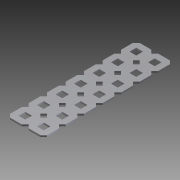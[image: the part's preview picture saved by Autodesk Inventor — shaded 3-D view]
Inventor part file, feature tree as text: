
AUTODESK INVENTOR PART (.ipt)
format: ipt  version: 2014 SP1 (Build 180222100, 222)  size: 609,792 bytes
history: native  units: in
note: dims shown in document units (in); Inventor stores cm internally (conversion verified against a paired STEP export)
features: extrude x2, sketch x2, other x1, imported_body x1
ambient origin geometry x8: Origin, YZ Plane, XZ Plane, XY Plane, X Axis, Y Axis, Z Axis, Center Point
bodies: Body1 (feature_tree)
feature tree (6):
  parser-record x1  (decoder bookkeeping rows leaked as tree rows — omitted from the tree; the rows remain in map.json)
  imported_body  "Base1"
  extrude  "Extrusion1"  Depth=1.0in TaperAngle=0.0deg
  extrude  "Extrusion2"  Depth=1.5in
  sketch  "Sketch1"  dims[d0=1.5in d1=1.0in d2=0.0in]
  sketch  "Sketch2"  dims[d3=1.0in d4=0.0in d5=1.5in]
